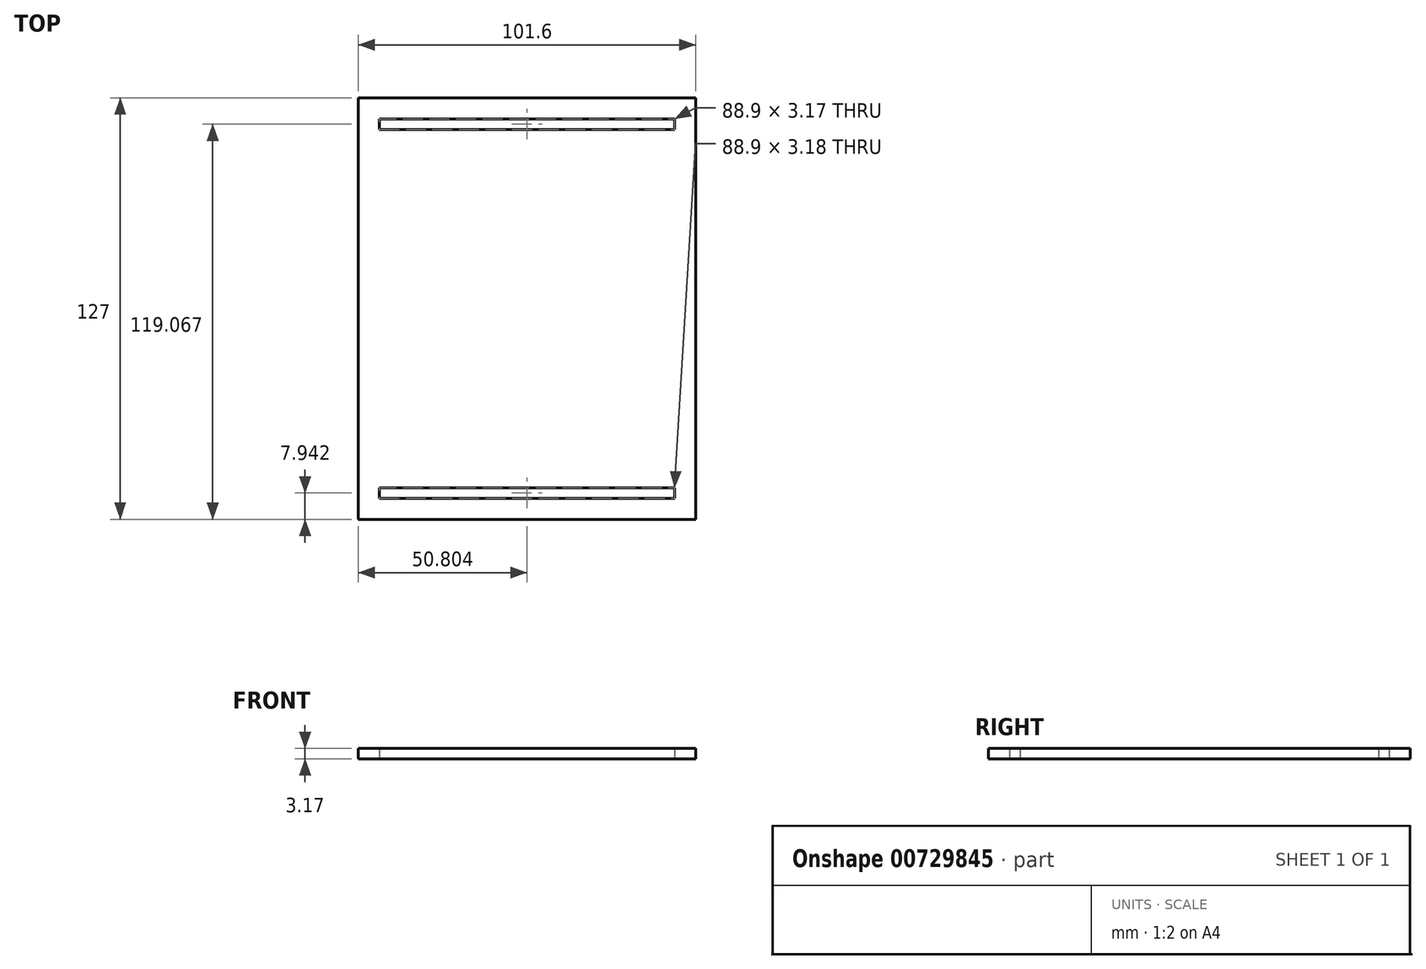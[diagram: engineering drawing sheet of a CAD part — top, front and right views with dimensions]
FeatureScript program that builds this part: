
annotation { "Feature Type Name" : "Feature", "Feature Type Description" : "" }
export const myFeature = defineFeature(function(context is Context, id is Id, definition is map)
    precondition{}
    {
        {
            var Q0;
            Q0=qCreatedBy(makeId("Top.planeOp"),FACE);
            var sketch = newSketch(context, id + "F0", { "sketchPlane" : qUnion([Q0])});
            skLineSegment(sketch, "E0.bottom", {"start": v(-46.54, 117.17) * mm, "end": v(55.06, 117.17) * mm});
            skLineSegment(sketch, "E0.top", {"start": v(-46.54, -9.83) * mm, "end": v(55.06, -9.83) * mm});
            skLineSegment(sketch, "E0.left", {"start": v(-46.54, 117.17) * mm, "end": v(-46.54, -9.83) * mm});
            skLineSegment(sketch, "E0.right", {"start": v(55.06, 117.17) * mm, "end": v(55.06, -9.83) * mm});
            skLineSegment(sketch, "E1.bottom", {"start": v(-46.54, 117.17) * mm, "end": v(-40.19, 117.17) * mm});
            skLineSegment(sketch, "E1.top", {"start": v(-46.54, 110.82) * mm, "end": v(-40.19, 110.82) * mm});
            skLineSegment(sketch, "E1.left", {"start": v(-46.54, 117.17) * mm, "end": v(-46.54, 110.82) * mm});
            skLineSegment(sketch, "E1.right", {"start": v(-40.19, 117.17) * mm, "end": v(-40.19, 110.82) * mm});
            skLineSegment(sketch, "E2.bottom", {"start": v(55.06, 117.17) * mm, "end": v(48.71, 117.17) * mm});
            skLineSegment(sketch, "E2.top", {"start": v(55.06, 110.82) * mm, "end": v(48.71, 110.82) * mm});
            skLineSegment(sketch, "E2.left", {"start": v(55.06, 117.17) * mm, "end": v(55.06, 110.82) * mm});
            skLineSegment(sketch, "E2.right", {"start": v(48.71, 117.17) * mm, "end": v(48.71, 110.82) * mm});
            skLineSegment(sketch, "E3.bottom", {"start": v(-40.19, 110.82) * mm, "end": v(48.71, 110.82) * mm});
            skLineSegment(sketch, "E3.top", {"start": v(-40.19, 107.65) * mm, "end": v(48.71, 107.65) * mm});
            skLineSegment(sketch, "E3.left", {"start": v(-40.19, 110.82) * mm, "end": v(-40.19, 107.65) * mm});
            skLineSegment(sketch, "E3.right", {"start": v(48.71, 110.82) * mm, "end": v(48.71, 107.65) * mm});
            skLineSegment(sketch, "E4.bottom", {"start": v(-46.54, -9.83) * mm, "end": v(-40.19, -9.83) * mm});
            skLineSegment(sketch, "E4.top", {"start": v(-46.54, -3.48) * mm, "end": v(-40.19, -3.48) * mm});
            skLineSegment(sketch, "E4.left", {"start": v(-46.54, -9.83) * mm, "end": v(-46.54, -3.48) * mm});
            skLineSegment(sketch, "E4.right", {"start": v(-40.19, -9.83) * mm, "end": v(-40.19, -3.48) * mm});
            skLineSegment(sketch, "E5.bottom", {"start": v(55.06, -9.83) * mm, "end": v(48.71, -9.83) * mm});
            skLineSegment(sketch, "E5.top", {"start": v(55.06, -3.48) * mm, "end": v(48.71, -3.48) * mm});
            skLineSegment(sketch, "E5.left", {"start": v(55.06, -9.83) * mm, "end": v(55.06, -3.48) * mm});
            skLineSegment(sketch, "E5.right", {"start": v(48.71, -9.83) * mm, "end": v(48.71, -3.48) * mm});
            skLineSegment(sketch, "E6.bottom", {"start": v(48.71, -3.48) * mm, "end": v(-40.19, -3.48) * mm});
            skLineSegment(sketch, "E6.top", {"start": v(48.71, -0.3) * mm, "end": v(-40.19, -0.3) * mm});
            skLineSegment(sketch, "E6.left", {"start": v(48.71, -3.48) * mm, "end": v(48.71, -0.3) * mm});
            skLineSegment(sketch, "E6.right", {"start": v(-40.19, -3.48) * mm, "end": v(-40.19, -0.3) * mm});
            skLineSegment(sketch, "E7.bottom", {"start": v(-46.54, -9.83) * mm, "end": v(4.26, -9.83) * mm});
            skLineSegment(sketch, "E8.bottom", {"start": v(-46.54, 117.17) * mm, "end": v(86.81, 117.17) * mm});
            skSolve(sketch);
        }
        {
            var Q0;
            Q0=qSketchRegion(id+"F0",true);
            var Q1;
            {var subQ0=sQuery(id+"F0.wireOp",EDGE,"E1.right");Q1=makeQuery(id+"F0.imprint","IMPRINT",FACE,{"disambiguationData":[TD([[makeQuery(id+"F0.imprint","IMPRINT",EDGE,{"derivedFrom":subQ0}),1.0]])]});}
            extrude(context, id + "F1", {"entities" : qUnion([Q0, Q1]), "depth" : 3.17 * mm, "offsetDistance" : 25.4 * mm});
        }
    });
